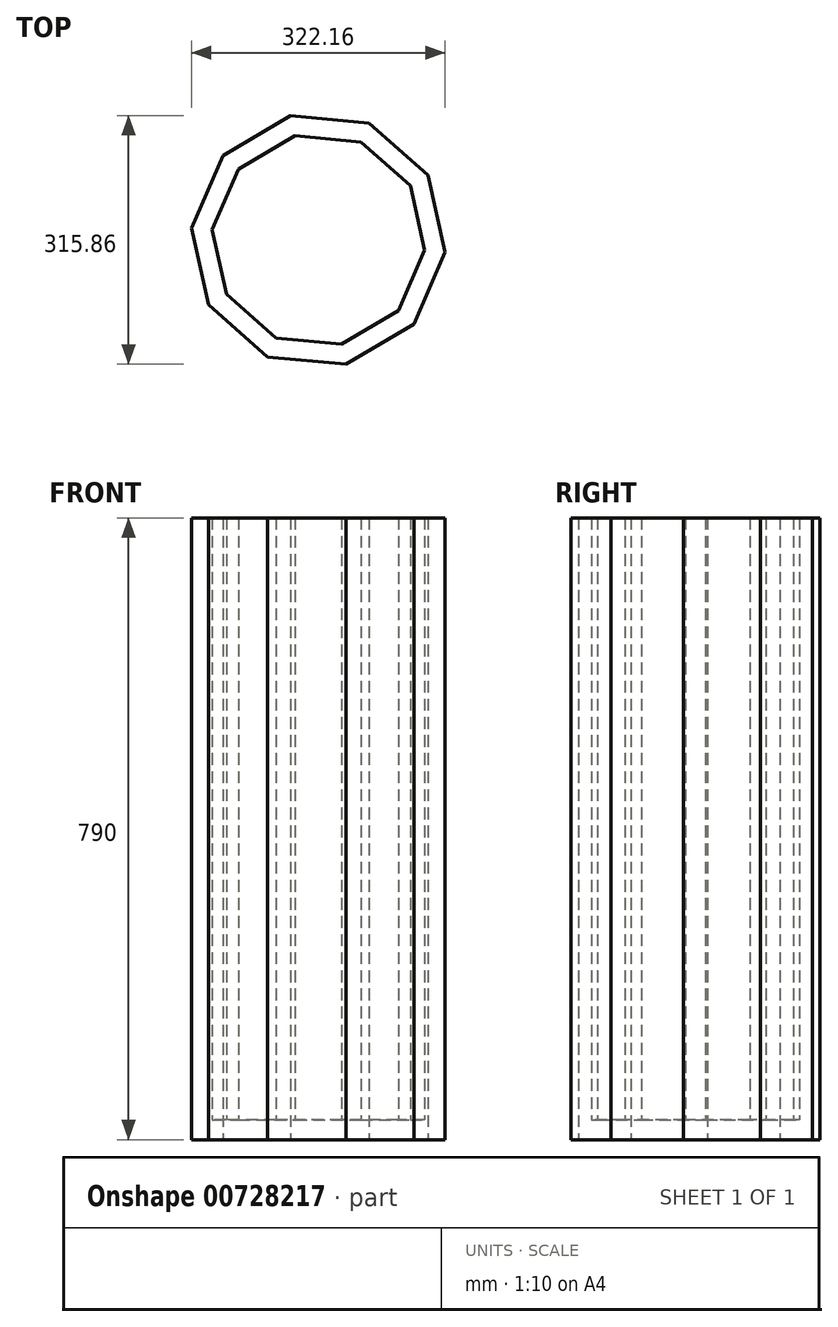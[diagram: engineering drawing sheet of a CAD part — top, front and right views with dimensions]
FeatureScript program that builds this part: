
annotation { "Feature Type Name" : "Feature", "Feature Type Description" : "" }
export const myFeature = defineFeature(function(context is Context, id is Id, definition is map)
    precondition{}
    {
        {
            var Q0;
            Q0=qCreatedBy(makeId("Top.planeOp"),FACE);
            var sketch = newSketch(context, id + "F0", { "sketchPlane" : qUnion([Q0])});
            skCircle(sketch, "E0.cCircle", {"center": v(0, 0) * mm, "radius": 153.88 * mm, "construction": true});
            skLineSegment(sketch, "E0.0", {"start": v(121.3, -107.08) * mm, "end": v(35.2, -157.93) * mm});
            skLineSegment(sketch, "E0.1", {"start": v(35.2, -157.93) * mm, "end": v(-64.36, -148.45) * mm});
            skLineSegment(sketch, "E0.2", {"start": v(-64.36, -148.45) * mm, "end": v(-139.33, -82.27) * mm});
            skLineSegment(sketch, "E0.3", {"start": v(-139.33, -82.27) * mm, "end": v(-161.08, 15.33) * mm});
            skLineSegment(sketch, "E0.4", {"start": v(-161.08, 15.33) * mm, "end": v(-121.3, 107.08) * mm});
            skLineSegment(sketch, "E0.5", {"start": v(-121.3, 107.08) * mm, "end": v(-35.2, 157.93) * mm});
            skLineSegment(sketch, "E0.6", {"start": v(-35.2, 157.93) * mm, "end": v(64.36, 148.45) * mm});
            skLineSegment(sketch, "E0.7", {"start": v(64.36, 148.45) * mm, "end": v(139.33, 82.27) * mm});
            skLineSegment(sketch, "E0.8", {"start": v(139.33, 82.27) * mm, "end": v(161.08, -15.33) * mm});
            skLineSegment(sketch, "E0.9", {"start": v(161.08, -15.33) * mm, "end": v(121.3, -107.08) * mm});
            skPoint(sketch, "E0.0.midPoint", {"position": v(78.25, -132.5) * mm});
            skSolve(sketch);
        }
        {
            var Q0;
            Q0 = qSketchRegion(id + "F0", true);
            extrude(context, id + "F1", {"entities" : qUnion([Q0]), "depth" : 790 * mm, "offsetDistance" : 25 * mm});
        }
        {
            var Q0;
            Q0=makeQuery(id+"F1.opExtrude","CAP_FACE",FACE,{"disambiguationData":[OSD([sQuery(id+"F0.wireOp",EDGE,"E0.0"),sQuery(id+"F0.wireOp",EDGE,"E0.1"),sQuery(id+"F0.wireOp",EDGE,"E0.2"),sQuery(id+"F0.wireOp",EDGE,"E0.3"),sQuery(id+"F0.wireOp",EDGE,"E0.4"),sQuery(id+"F0.wireOp",EDGE,"E0.5"),sQuery(id+"F0.wireOp",EDGE,"E0.6"),sQuery(id+"F0.wireOp",EDGE,"E0.7"),sQuery(id+"F0.wireOp",EDGE,"E0.8"),sQuery(id+"F0.wireOp",EDGE,"E0.9")])],"isStart":false});
            shell(context, id + "F2", {"entities" : qUnion([Q0]), "thickness" : 25 * mm});
        }
    });
